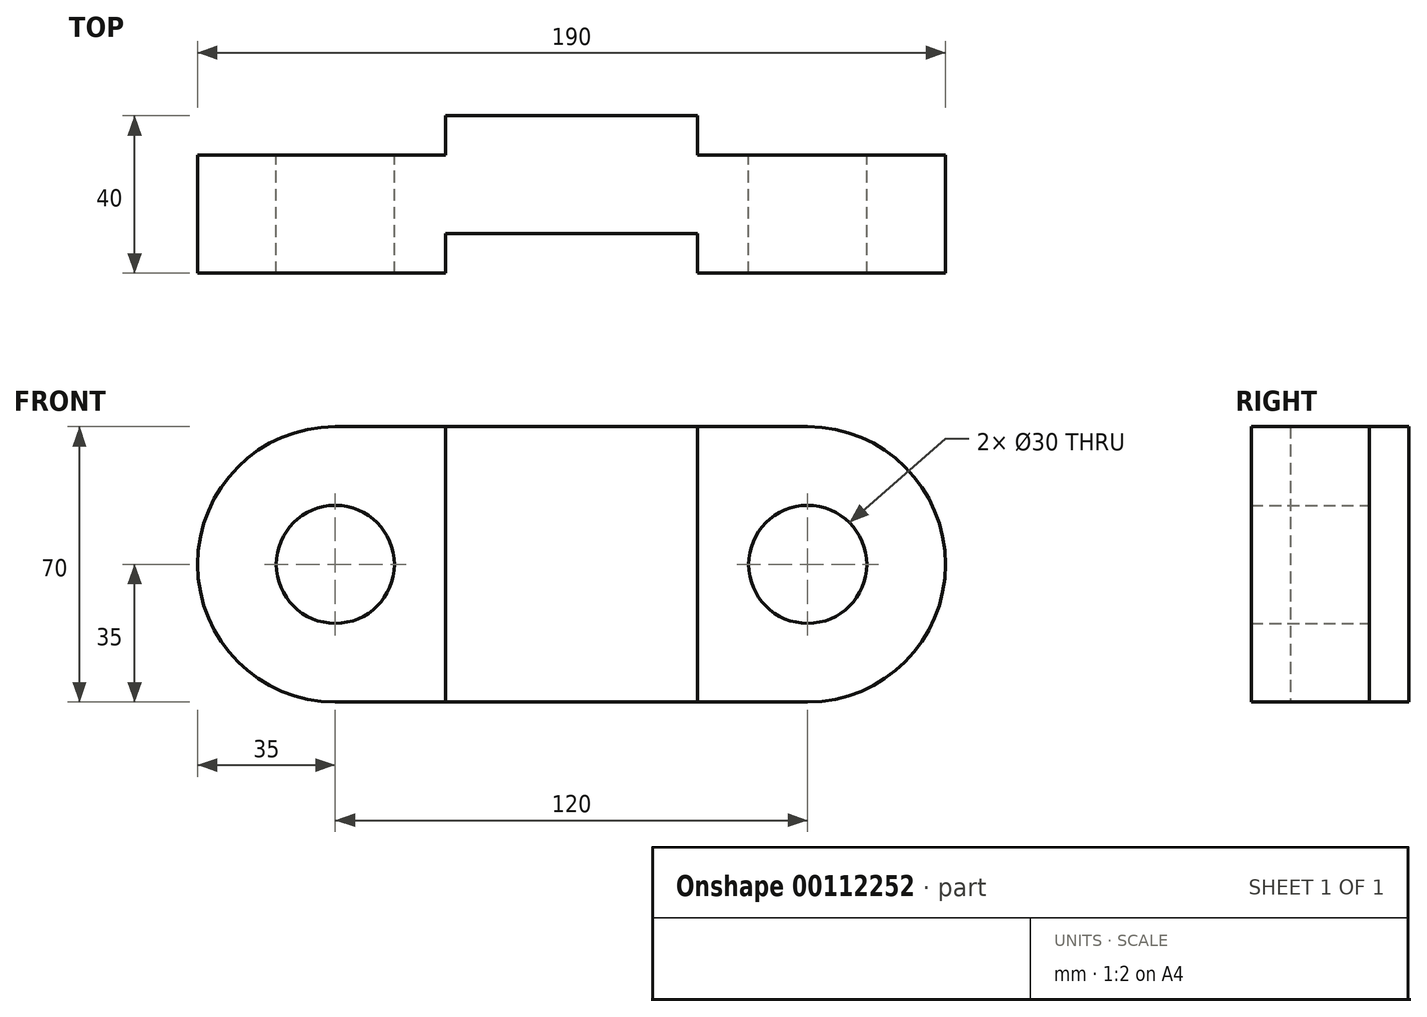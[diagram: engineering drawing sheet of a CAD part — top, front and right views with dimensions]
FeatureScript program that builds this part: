
annotation { "Feature Type Name" : "Feature", "Feature Type Description" : "" }
export const myFeature = defineFeature(function(context is Context, id is Id, definition is map)
    precondition{}
    {
        {
            var Q0;
            Q0=qCreatedBy(makeId("Front.planeOp"),FACE);
            var sketch = newSketch(context, id + "F0", { "sketchPlane" : qUnion([Q0])});
            skLineSegment(sketch, "E0.top", {"start": v(60, 35) * mm, "end": v(-60, 35) * mm});
            skLineSegment(sketch, "E0.left", {"start": v(95, 0) * mm, "end": v(95, 0) * mm});
            skLineSegment(sketch, "E0.right", {"start": v(-95, 0) * mm, "end": v(-95, 0) * mm});
            skPoint(sketch, "E0.middle", {"position": v(0, 0) * mm});
            skLineSegment(sketch, "E1", {"start": v(0, 35) * mm, "end": v(0, -35) * mm});
            skPoint(sketch, "E2.orphan", {"position": v(-47.5, -35) * mm});
            skPoint(sketch, "E3.orphan", {"position": v(-95, 0) * mm});
            skPoint(sketch, "E4.orphan", {"position": v(-47.5, 35) * mm});
            skLineSegment(sketch, "E5", {"start": v(-60, -35) * mm, "end": v(60, -35) * mm});
            skPoint(sketch, "E6.orphan", {"position": v(47.5, 35) * mm});
            skPoint(sketch, "E7.orphan", {"position": v(95, 0) * mm});
            skPoint(sketch, "E8.orphan", {"position": v(47.5, -35) * mm});
            skPoint(sketch, "E9.visualSharp", {"position": v(-95, -35) * mm});
            skArc(sketch, "E9.filletArc", {"start": v(-95, 0) * mm, "mid": v(-84.75, -24.75) * mm, "end": v(-60, -35) * mm});
            skPoint(sketch, "E10.visualSharp", {"position": v(-95, 35) * mm});
            skArc(sketch, "E10.filletArc", {"start": v(-60, 35) * mm, "mid": v(-84.75, 24.75) * mm, "end": v(-95, 0) * mm});
            skPoint(sketch, "E11.visualSharp", {"position": v(95, 35) * mm});
            skArc(sketch, "E11.filletArc", {"start": v(95, 0) * mm, "mid": v(84.75, 24.75) * mm, "end": v(60, 35) * mm});
            skPoint(sketch, "E12.visualSharp", {"position": v(95, -35) * mm});
            skArc(sketch, "E12.filletArc", {"start": v(60, -35) * mm, "mid": v(84.75, -24.75) * mm, "end": v(95, 0) * mm});
            skLineSegment(sketch, "E13", {"start": v(-32, -35) * mm, "end": v(-32, 35) * mm});
            skLineSegment(sketch, "E14", {"start": v(32, -35) * mm, "end": v(32, 35) * mm});
            skPoint(sketch, "E15.center.orphan", {"position": v(-47.5, 0) * mm});
            skPoint(sketch, "E16.center.orphan", {"position": v(47.5, 0) * mm});
            skCircle(sketch, "E17", {"center": v(-60, 0) * mm, "radius": 15 * mm});
            skCircle(sketch, "E18", {"center": v(60, 0) * mm, "radius": 15 * mm});
            skSolve(sketch);
        }
        {
            var Q0;
            {var subQ3=sQuery(id+"F0.wireOp",EDGE,"E9.filletArc");Q0=makeQuery(id+"F0.imprint","IMPRINT",FACE,{"disambiguationData":[TD([[makeQuery(id+"F0.imprint","IMPRINT",EDGE,{"derivedFrom":subQ3}),1.0]])]});}
            var Q1;
            {var subQ0=sQuery(id+"F0.wireOp",EDGE,"E1");Q1=makeQuery(id+"F0.imprint","IMPRINT",FACE,{"disambiguationData":[TD([[makeQuery(id+"F0.imprint","IMPRINT",EDGE,{"derivedFrom":subQ0}),-1.0]])]});}
            var Q2;
            {var subQ0=sQuery(id+"F0.wireOp",EDGE,"E1");Q2=makeQuery(id+"F0.imprint","IMPRINT",FACE,{"disambiguationData":[TD([[makeQuery(id+"F0.imprint","IMPRINT",EDGE,{"derivedFrom":subQ0}),1.0]])]});}
            var Q3;
            {var subQ1=sQuery(id+"F0.wireOp",EDGE,"E11.filletArc");Q3=makeQuery(id+"F0.imprint","IMPRINT",FACE,{"disambiguationData":[TD([[makeQuery(id+"F0.imprint","IMPRINT",EDGE,{"derivedFrom":subQ1}),1.0]])]});}
            extrude(context, id + "F1", {"entities" : qUnion([Q0, Q1, Q2, Q3]), "depth" : 30 * mm});
        }
        {
            var Q0;
            Q0=makeQuery(id+"F1.opExtrude","CAP_FACE",FACE,{"disambiguationData":[OSD([sQuery(id+"F0.wireOp",EDGE,"E0.top"),sQuery(id+"F0.wireOp",EDGE,"E5"),sQuery(id+"F0.wireOp",EDGE,"E9.filletArc"),sQuery(id+"F0.wireOp",EDGE,"E10.filletArc"),sQuery(id+"F0.wireOp",EDGE,"E11.filletArc"),sQuery(id+"F0.wireOp",EDGE,"E12.filletArc"),sQuery(id+"F0.wireOp",EDGE,"E17"),sQuery(id+"F0.wireOp",EDGE,"E18")])],"isStart":false});
            var sketch = newSketch(context, id + "F2", { "sketchPlane" : qUnion([Q0])});
            skLineSegment(sketch, "E19", {"start": v(-32, 35) * mm, "end": v(-32, -35) * mm});
            skLineSegment(sketch, "E20", {"start": v(32, 35) * mm, "end": v(32, -35) * mm});
            skSolve(sketch);
        }
        {
            var Q0;
            {var subQ0=sQuery(id+"F2.wireOp",EDGE,"E19");Q0=makeQuery(id+"F2.imprint","IMPRINT",FACE,{"disambiguationData":[TD([[makeQuery(id+"F2.imprint","IMPRINT",EDGE,{"derivedFrom":subQ0}),1.0]])]});}
            extrude(context, id + "F3", {"entities" : qUnion([Q0]), "operationType" : NewBodyOperationType.REMOVE, "oppositeDirection" : true, "depth" : 10 * mm});
        }
        {
            var Q0;
            Q0=makeQuery(id+"F1.opExtrude","CAP_FACE",FACE,{"disambiguationData":[OSD([sQuery(id+"F0.wireOp",EDGE,"E0.top"),sQuery(id+"F0.wireOp",EDGE,"E5"),sQuery(id+"F0.wireOp",EDGE,"E9.filletArc"),sQuery(id+"F0.wireOp",EDGE,"E10.filletArc"),sQuery(id+"F0.wireOp",EDGE,"E11.filletArc"),sQuery(id+"F0.wireOp",EDGE,"E12.filletArc"),sQuery(id+"F0.wireOp",EDGE,"E17"),sQuery(id+"F0.wireOp",EDGE,"E18")])],"isStart":true});
            var sketch = newSketch(context, id + "F4", { "sketchPlane" : qUnion([Q0])});
            skLineSegment(sketch, "E21", {"start": v(-32, 35) * mm, "end": v(-32, -35) * mm});
            skLineSegment(sketch, "E22", {"start": v(32, 35) * mm, "end": v(32, -35) * mm});
            skSolve(sketch);
        }
        {
            var Q0;
            {var subQ0=sQuery(id+"F4.wireOp",EDGE,"E21");Q0=makeQuery(id+"F4.imprint","IMPRINT",FACE,{"disambiguationData":[TD([[makeQuery(id+"F4.imprint","IMPRINT",EDGE,{"derivedFrom":subQ0}),1.0]])]});}
            extrude(context, id + "F5", {"entities" : qUnion([Q0]), "operationType" : NewBodyOperationType.ADD, "depth" : 10 * mm});
        }
    });
